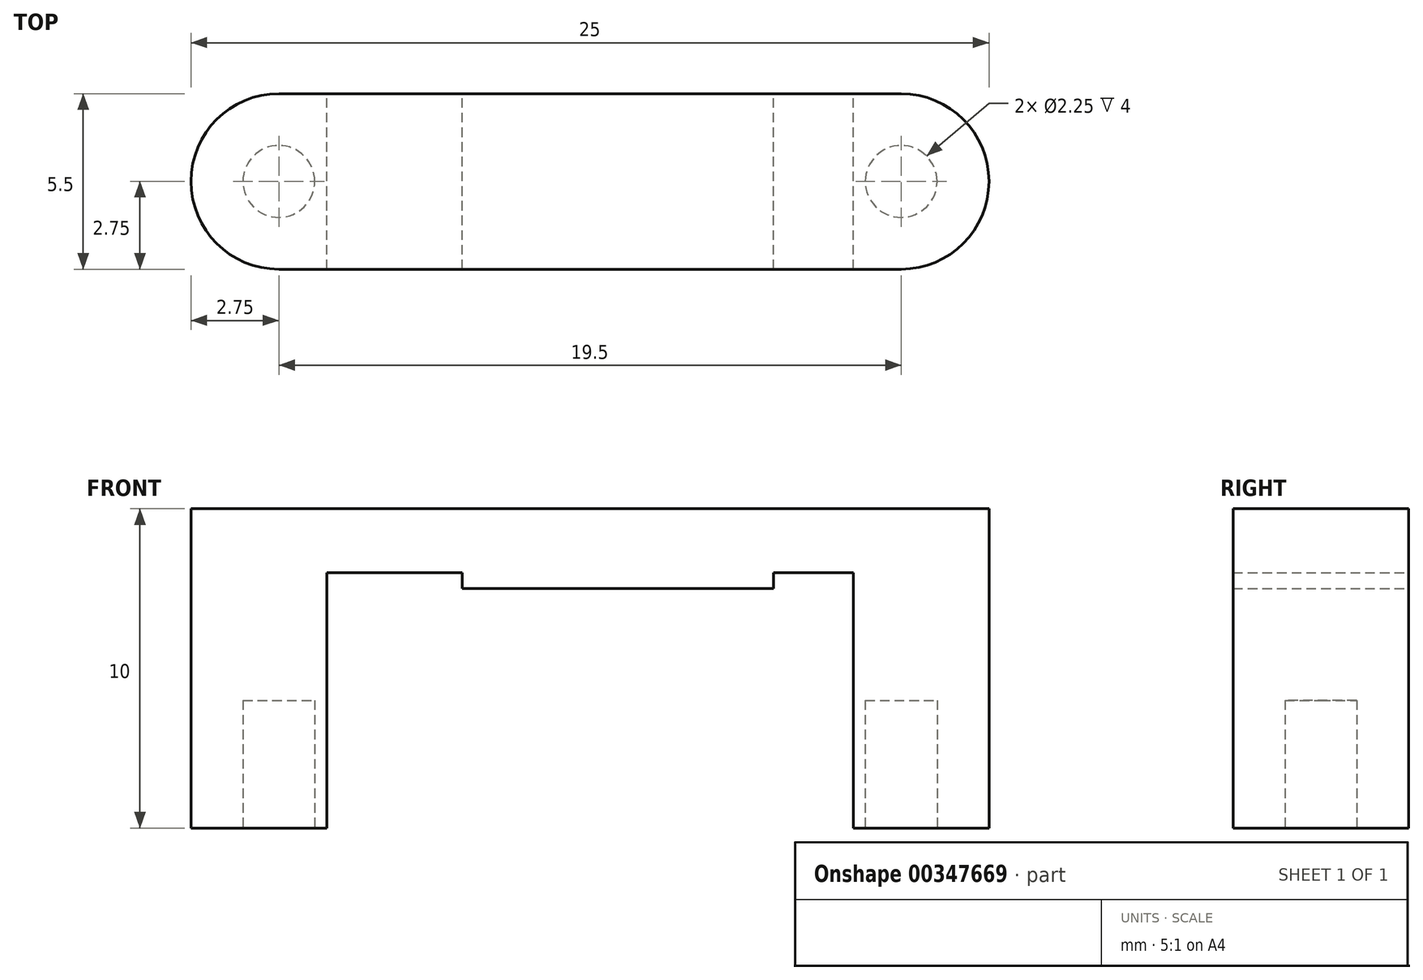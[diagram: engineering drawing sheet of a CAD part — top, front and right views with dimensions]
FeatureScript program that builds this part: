
annotation { "Feature Type Name" : "Feature", "Feature Type Description" : "" }
export const myFeature = defineFeature(function(context is Context, id is Id, definition is map)
    precondition{}
    {
        {
            var Q0;
            Q0=qCreatedBy(makeId("Front.planeOp"),FACE);
            var sketch = newSketch(context, id + "F0", { "sketchPlane" : qUnion([Q0])});
            skLineSegment(sketch, "E0.bottom", {"start": v(-12.5, 0) * mm, "end": v(-8.25, 0) * mm});
            skLineSegment(sketch, "E0.top", {"start": v(-12.5, 10) * mm, "end": v(12.5, 10) * mm});
            skLineSegment(sketch, "E0.left", {"start": v(-12.5, 0) * mm, "end": v(-12.5, 10) * mm});
            skLineSegment(sketch, "E0.right", {"start": v(12.5, 0) * mm, "end": v(12.5, 10) * mm});
            skLineSegment(sketch, "E1.top", {"start": v(-8.25, 8) * mm, "end": v(-4, 8) * mm});
            skLineSegment(sketch, "E1.left", {"start": v(-8.25, 0) * mm, "end": v(-8.25, 8) * mm});
            skLineSegment(sketch, "E1.right", {"start": v(8.25, 0) * mm, "end": v(8.25, 8) * mm});
            skLineSegment(sketch, "E2.trimOffspring", {"start": v(8.25, 0) * mm, "end": v(12.5, 0) * mm});
            skLineSegment(sketch, "E3", {"start": v(-4, 8) * mm, "end": v(-4, 7.5) * mm});
            skLineSegment(sketch, "E4", {"start": v(-4, 7.5) * mm, "end": v(5.75, 7.5) * mm});
            skLineSegment(sketch, "E5", {"start": v(5.75, 7.5) * mm, "end": v(5.75, 8) * mm});
            skLineSegment(sketch, "E6.trimOffspring", {"start": v(5.75, 8) * mm, "end": v(8.25, 8) * mm});
            skSolve(sketch);
        }
        {
            var Q0;
            Q0=makeQuery(id+"F0.imprint","IMPRINT",FACE,{"disambiguationData":[TD([[makeQuery(id+"F0.imprint","IMPRINT",EDGE,{"derivedFrom":sQuery(id+"F0.wireOp",EDGE,"E0.bottom")}),1.0]])]});
            extrude(context, id + "F1", {"entities" : qUnion([Q0]), "depth" : 5.5 * mm});
        }
        {
            var Q0;
            Q0=makeQuery(id+"F1.opExtrude","SWEPT_FACE",FACE,{"disambiguationData":[OSD([sQuery(id+"F0.wireOp",EDGE,"E0.bottom")])]});
            var sketch = newSketch(context, id + "F2", { "sketchPlane" : qUnion([Q0])});
            skCircle(sketch, "E7", {"center": v(-9.75, 2.75) * mm, "radius": 1.13 * mm});
            skCircle(sketch, "E8", {"center": v(9.75, 2.75) * mm, "radius": 1.13 * mm});
            skPoint(sketch, "E8.centerSnap0", {"position": v(-8.25, 2.75) * mm});
            skSolve(sketch);
        }
        {
            var Q0;
            Q0 = qSketchRegion(id + "F2", true);
            extrude(context, id + "F3", {"entities" : qUnion([Q0]), "operationType" : NewBodyOperationType.REMOVE, "oppositeDirection" : true, "depth" : 4 * mm});
        }
        {
            var Q0;
            Q0=makeQuery(id+"F1.opExtrude","CAP_EDGE",EDGE,{"disambiguationData":[OSD([sQuery(id+"F0.wireOp",EDGE,"E0.left")])],"isStart":false});
            var Q1;
            Q1=makeQuery(id+"F1.opExtrude","CAP_EDGE",EDGE,{"disambiguationData":[OSD([sQuery(id+"F0.wireOp",EDGE,"E0.left")])],"isStart":true});
            var Q2;
            Q2=makeQuery(id+"F1.opExtrude","CAP_EDGE",EDGE,{"disambiguationData":[OSD([sQuery(id+"F0.wireOp",EDGE,"E0.right")])],"isStart":false});
            var Q3;
            Q3=makeQuery(id+"F1.opExtrude","CAP_EDGE",EDGE,{"disambiguationData":[OSD([sQuery(id+"F0.wireOp",EDGE,"E0.right")])],"isStart":true});
            fillet(context, id + "F4", {"entities" : qUnion([Q0, Q1, Q2, Q3]), "radius" : 2.75 * mm, "tangentPropagation" : true, "allowEdgeOverflow" : false});
        }
    });
